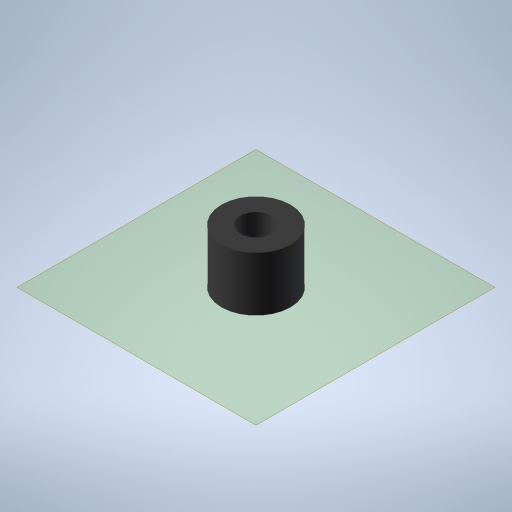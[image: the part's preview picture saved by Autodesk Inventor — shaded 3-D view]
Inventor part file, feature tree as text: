
AUTODESK INVENTOR PART (.ipt)
format: ipt  version: 2024 (Build 280153000, 153)  size: 247,808 bytes
history: native  units: in
note: dims shown in document units (in); Inventor stores cm internally (conversion verified against a paired STEP export)
features: plane x1, extrude x1, sketch x1
ambient origin geometry x8: Origin, YZ Plane, XZ Plane, XY Plane, X Axis, Y Axis, Z Axis, Center Point
bodies: Body1 (feature_tree)
feature tree (3):
  plane  "Work Plane1"
  extrude  "Extrusion1"  [1 undecoded]
  sketch  "Sketch1"  dims[d0=0.1969in d1=0.0in]
note: 1 required parameter value undecoded (feature->parameter linkage not recoverable at this tier; creation-order binding heuristic only, values carry confidence <= 0.55)
